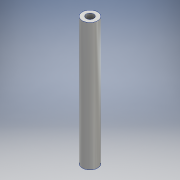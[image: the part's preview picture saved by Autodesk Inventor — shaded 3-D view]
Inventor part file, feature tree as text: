
AUTODESK INVENTOR PART (.ipt)
format: ipt  version: 2016 (Build 200138000, 138)  size: 92,672 bytes
history: native  units: mm
features: other x1, extrude x1, sketch x1
ambient origin geometry x8: Origin, YZ Plane, XZ Plane, XY Plane, X Axis, Y Axis, Z Axis, Center Point
bodies: Body1 (feature_tree)
feature tree (3):
  other  "ソリッド1"
  extrude  "押し出し1"  Depth=6.0mm
  sketch  "スケッチ1"
